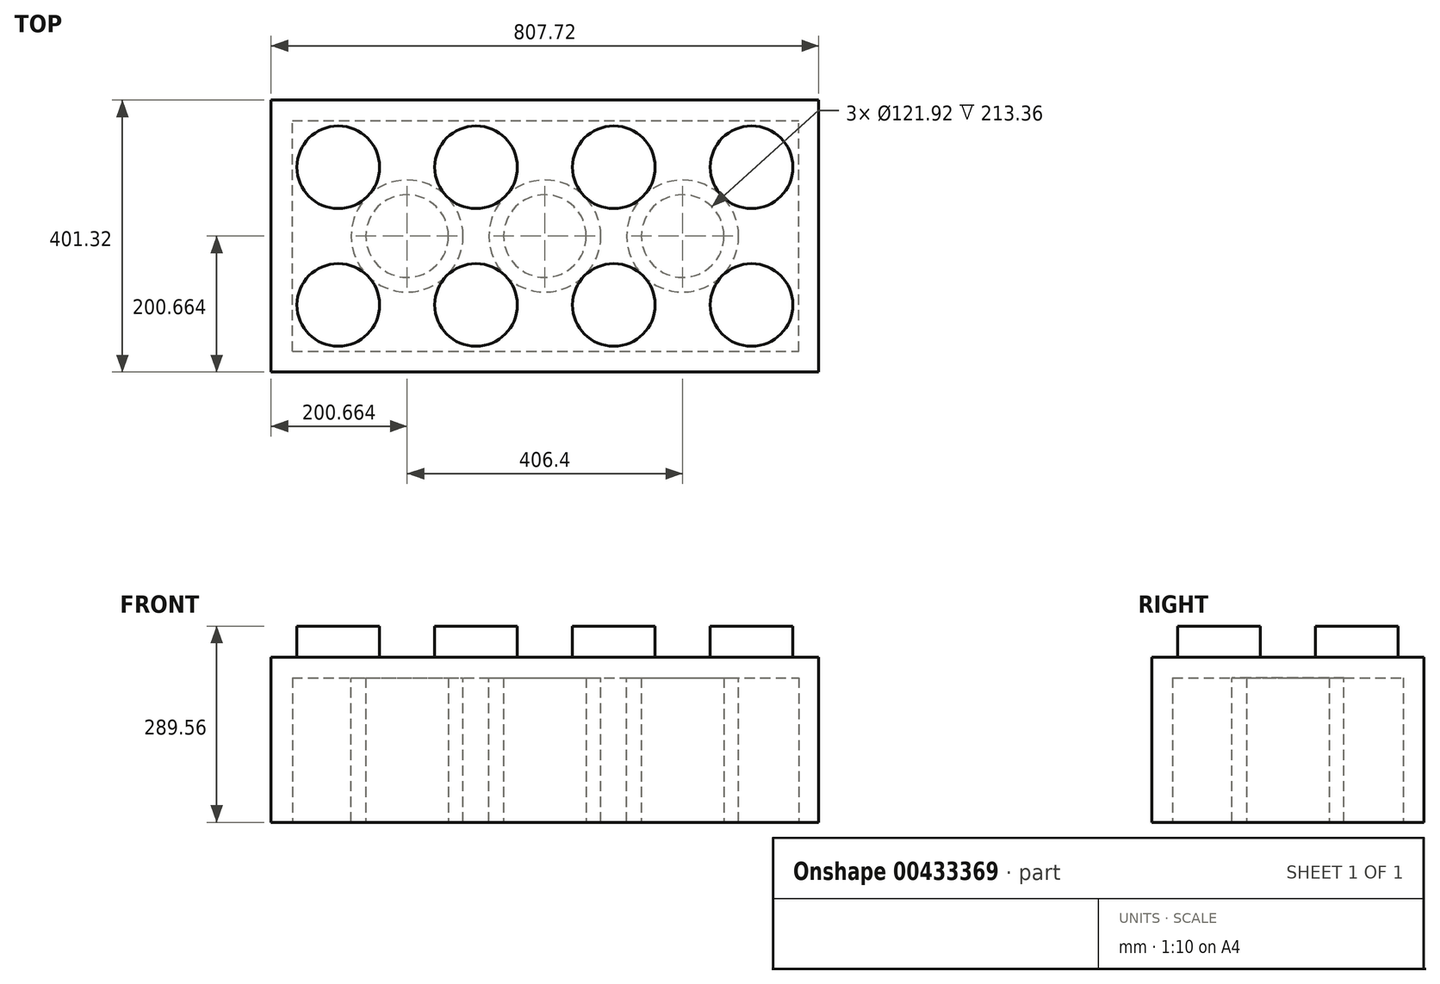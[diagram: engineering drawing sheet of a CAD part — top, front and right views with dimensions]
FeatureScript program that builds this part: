
annotation { "Feature Type Name" : "Feature", "Feature Type Description" : "" }
export const myFeature = defineFeature(function(context is Context, id is Id, definition is map)
    precondition{}
    {
        {
            var Q0;
            Q0=qCreatedBy(makeId("Top.planeOp"),FACE);
            var sketch = newSketch(context, id + "F0", { "sketchPlane" : qUnion([Q0])});
            skLineSegment(sketch, "E0.bottom", {"start": v(-406.83, 196.66) * mm, "end": v(400.9, 196.66) * mm});
            skLineSegment(sketch, "E0.top", {"start": v(-406.83, -204.66) * mm, "end": v(400.9, -204.66) * mm});
            skLineSegment(sketch, "E0.left", {"start": v(-406.83, 196.66) * mm, "end": v(-406.83, -204.66) * mm});
            skLineSegment(sketch, "E0.right", {"start": v(400.9, 196.66) * mm, "end": v(400.9, -204.66) * mm});
            skSolve(sketch);
        }
        {
            var Q0;
            Q0=qSketchRegion(id+"F0",true);
            extrude(context, id + "F1", {"entities" : qUnion([Q0]), "depth" : 243.84 * mm});
        }
        {
            var Q0;
            Q0=makeQuery(id+"F1.opExtrude","CAP_FACE",FACE,{"disambiguationData":[OSD([sQuery(id+"F0.wireOp",EDGE,"E0.bottom"),sQuery(id+"F0.wireOp",EDGE,"E0.top"),sQuery(id+"F0.wireOp",EDGE,"E0.left"),sQuery(id+"F0.wireOp",EDGE,"E0.right")])],"isStart":false});
            var sketch = newSketch(context, id + "F2", { "sketchPlane" : qUnion([Q0])});
            skCircle(sketch, "E1", {"center": v(-307.77, 97.6) * mm, "radius": 60.96 * mm});
            skCircle(sketch, "E2.0.1.0", {"center": v(-307.77, -105.6) * mm, "radius": 60.96 * mm});
            skCircle(sketch, "E2.1.0.0", {"center": v(-104.57, 97.6) * mm, "radius": 60.96 * mm});
            skCircle(sketch, "E2.1.1.0", {"center": v(-104.57, -105.6) * mm, "radius": 60.96 * mm});
            skCircle(sketch, "E2.2.0.0", {"center": v(98.63, 97.6) * mm, "radius": 60.96 * mm});
            skCircle(sketch, "E2.2.1.0", {"center": v(98.63, -105.6) * mm, "radius": 60.96 * mm});
            skCircle(sketch, "E2.3.0.0", {"center": v(301.83, 97.6) * mm, "radius": 60.96 * mm});
            skCircle(sketch, "E2.3.1.0", {"center": v(301.83, -105.6) * mm, "radius": 60.96 * mm});
            skLineSegment(sketch, "E2.direction1", {"start": v(-307.77, 97.6) * mm, "end": v(-104.57, 97.6) * mm, "construction": true});
            skLineSegment(sketch, "E2.direction2", {"start": v(-307.77, 97.6) * mm, "end": v(-307.77, -105.6) * mm, "construction": true});
            skSolve(sketch);
        }
        {
            var Q0;
            Q0=makeQuery(id+"F2.imprint","IMPRINT",FACE,{"disambiguationData":[TD([[makeQuery(id+"F2.imprint","IMPRINT",EDGE,{"derivedFrom":sQuery(id+"F2.wireOp",EDGE,"E1")}),1.0]])]});
            var Q1;
            Q1=makeQuery(id+"F2.imprint","IMPRINT",FACE,{"disambiguationData":[TD([[makeQuery(id+"F2.imprint","IMPRINT",EDGE,{"derivedFrom":sQuery(id+"F2.wireOp",EDGE,"E2.0.1.0")}),1.0]])]});
            var Q2;
            Q2=makeQuery(id+"F2.imprint","IMPRINT",FACE,{"disambiguationData":[TD([[makeQuery(id+"F2.imprint","IMPRINT",EDGE,{"derivedFrom":sQuery(id+"F2.wireOp",EDGE,"E2.1.1.0")}),1.0]])]});
            var Q3;
            Q3=makeQuery(id+"F2.imprint","IMPRINT",FACE,{"disambiguationData":[TD([[makeQuery(id+"F2.imprint","IMPRINT",EDGE,{"derivedFrom":sQuery(id+"F2.wireOp",EDGE,"E2.1.0.0")}),1.0]])]});
            var Q4;
            Q4=makeQuery(id+"F2.imprint","IMPRINT",FACE,{"disambiguationData":[TD([[makeQuery(id+"F2.imprint","IMPRINT",EDGE,{"derivedFrom":sQuery(id+"F2.wireOp",EDGE,"E2.2.0.0")}),1.0]])]});
            var Q5;
            Q5=makeQuery(id+"F2.imprint","IMPRINT",FACE,{"disambiguationData":[TD([[makeQuery(id+"F2.imprint","IMPRINT",EDGE,{"derivedFrom":sQuery(id+"F2.wireOp",EDGE,"E2.2.1.0")}),1.0]])]});
            var Q6;
            Q6=makeQuery(id+"F2.imprint","IMPRINT",FACE,{"disambiguationData":[TD([[makeQuery(id+"F2.imprint","IMPRINT",EDGE,{"derivedFrom":sQuery(id+"F2.wireOp",EDGE,"E2.3.1.0")}),1.0]])]});
            var Q7;
            Q7=makeQuery(id+"F2.imprint","IMPRINT",FACE,{"disambiguationData":[TD([[makeQuery(id+"F2.imprint","IMPRINT",EDGE,{"derivedFrom":sQuery(id+"F2.wireOp",EDGE,"E2.3.0.0")}),1.0]])]});
            extrude(context, id + "F3", {"entities" : qUnion([Q0, Q1, Q2, Q3, Q4, Q5, Q6, Q7]), "operationType" : NewBodyOperationType.ADD, "depth" : 45.72 * mm});
        }
        {
            var Q0;
            Q0=makeQuery(id+"F1.opExtrude","CAP_FACE",FACE,{"disambiguationData":[OSD([sQuery(id+"F0.wireOp",EDGE,"E0.bottom"),sQuery(id+"F0.wireOp",EDGE,"E0.top"),sQuery(id+"F0.wireOp",EDGE,"E0.left"),sQuery(id+"F0.wireOp",EDGE,"E0.right")])],"isStart":true});
            var sketch = newSketch(context, id + "F4", { "sketchPlane" : qUnion([Q0])});
            skLineSegment(sketch, "E3.bottom", {"start": v(-375.37, 174.18) * mm, "end": v(371.39, 174.18) * mm});
            skLineSegment(sketch, "E3.top", {"start": v(-375.37, -166.18) * mm, "end": v(371.39, -166.18) * mm});
            skLineSegment(sketch, "E3.left", {"start": v(-375.37, 174.18) * mm, "end": v(-375.37, -166.18) * mm});
            skLineSegment(sketch, "E3.right", {"start": v(371.39, 174.18) * mm, "end": v(371.39, -166.18) * mm});
            skSolve(sketch);
        }
        {
            var Q0;
            Q0=makeQuery(id+"F4.imprint","IMPRINT",FACE,{"disambiguationData":[TD([[makeQuery(id+"F4.imprint","IMPRINT",EDGE,{"derivedFrom":sQuery(id+"F4.wireOp",EDGE,"E3.bottom")}),-1.0]])]});
            extrude(context, id + "F5", {"entities" : qUnion([Q0]), "operationType" : NewBodyOperationType.REMOVE, "oppositeDirection" : true, "depth" : 213.36 * mm});
        }
        {
            var Q0;
            Q0=makeQuery(id+"F5.boolean.opBoolean","COPY",FACE,{"derivedFrom":makeQuery(id+"F5.opExtrude","CAP_FACE",FACE,{"disambiguationData":[OSD([sQuery(id+"F4.wireOp",EDGE,"E3.bottom"),sQuery(id+"F4.wireOp",EDGE,"E3.top"),sQuery(id+"F4.wireOp",EDGE,"E3.left"),sQuery(id+"F4.wireOp",EDGE,"E3.right")])],"isStart":false})});
            var sketch = newSketch(context, id + "F6", { "sketchPlane" : qUnion([Q0])});
            skCircle(sketch, "E4", {"center": v(-206.17, 4) * mm, "radius": 82.55 * mm});
            skCircle(sketch, "E5.1.0.0", {"center": v(-2.97, 4) * mm, "radius": 82.55 * mm});
            skCircle(sketch, "E5.2.0.0", {"center": v(200.23, 4) * mm, "radius": 82.55 * mm});
            skLineSegment(sketch, "E5.direction1", {"start": v(-206.17, 4) * mm, "end": v(-2.97, 4) * mm, "construction": true});
            skSolve(sketch);
        }
        {
            var Q0;
            Q0=qSketchRegion(id+"F6",true);
            extrude(context, id + "F7", {"entities" : qUnion([Q0]), "operationType" : NewBodyOperationType.ADD, "depth" : 213.36 * mm});
        }
        {
            var Q0;
            Q0=makeQuery(id+"F7.opExtrude","CAP_FACE",FACE,{"disambiguationData":[OSD([sQuery(id+"F6.wireOp",EDGE,"E4")])],"isStart":false});
            var sketch = newSketch(context, id + "F8", { "sketchPlane" : qUnion([Q0])});
            skCircle(sketch, "E6", {"center": v(-206.17, 4) * mm, "radius": 60.96 * mm});
            skCircle(sketch, "E7.1.0.0", {"center": v(-2.97, 4) * mm, "radius": 60.96 * mm});
            skCircle(sketch, "E7.2.0.0", {"center": v(200.23, 4) * mm, "radius": 60.96 * mm});
            skLineSegment(sketch, "E7.direction1", {"start": v(-206.17, 4) * mm, "end": v(-2.97, 4) * mm, "construction": true});
            skSolve(sketch);
        }
        {
            var Q0;
            Q0=qSketchRegion(id+"F8",true);
            extrude(context, id + "F9", {"entities" : qUnion([Q0]), "operationType" : NewBodyOperationType.REMOVE, "oppositeDirection" : true, "depth" : 213.36 * mm});
        }
    });
